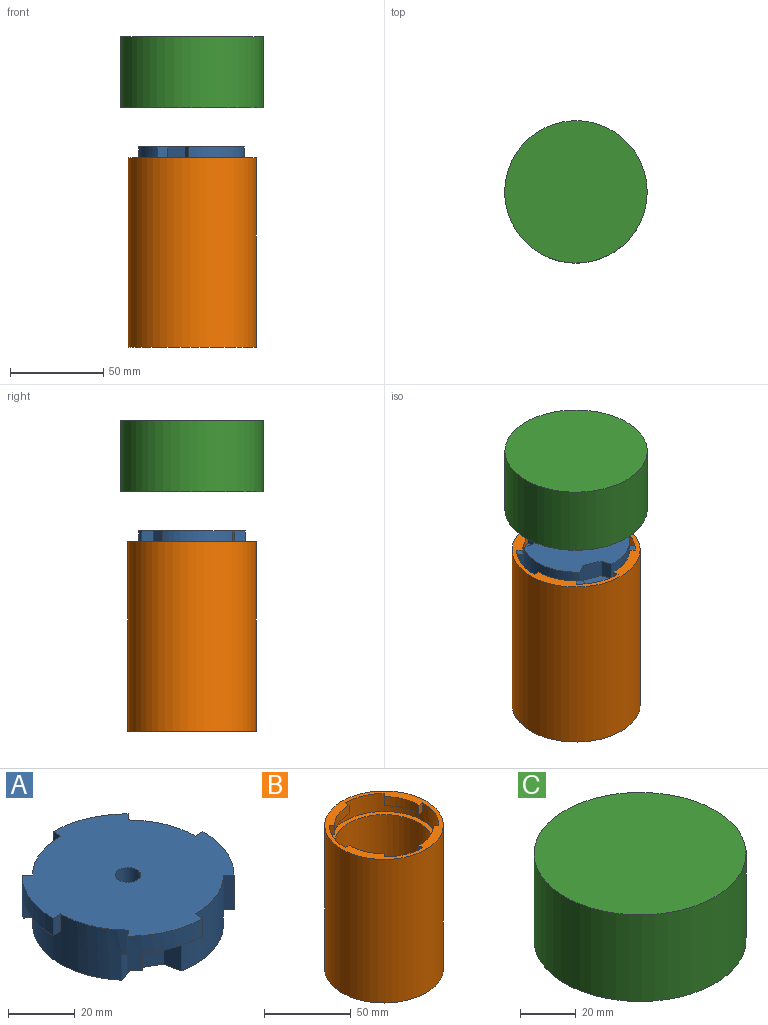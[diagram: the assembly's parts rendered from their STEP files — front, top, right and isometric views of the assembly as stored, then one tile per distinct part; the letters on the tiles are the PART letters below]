
ASSEMBLY  parts=3 mates=2
PART A: 43 faces, bbox 63.5x63.5x18.4 mm
  f0: cylinder r=28.57mm len=57.15mm, axis (0,0,-1), area 1491.7mm2, adj f2,f3,f8,f9,f11,f12,f18,f19
  f1: cylinder r=28.57mm len=39.03mm, axis (0,0,-1), area 629.9mm2, adj f4,f14,f15,f18,f20,f21,f27,f28
  f2: plane 19.11x8.93mm, normal (0,0,-1), area 61.8mm2, adj f0,f24,f32,f35
  f3: plane 19.11x8.93mm, normal (0,0,-1), area 61.8mm2, adj f0,f7,f30,f41
  f4: plane 19.11x8.93mm, normal (0,0,-1), area 61.8mm2, adj f1,f5,f28,f37
  f5: cylinder r=31.75mm len=22.45mm, axis (0,0,-1), area 186.5mm2, adj f4,f21,f28,f31,f37,f39
  f6: cylinder r=31.75mm len=22.45mm, axis (0,0,-1), area 186.5mm2, adj f21,f23,f26,f29,f33,f34
  f7: cylinder r=31.75mm len=22.45mm, axis (0,0,-1), area 186.5mm2, adj f3,f21,f27,f30,f41,f42
  f8: plane 9.53x6.24mm, normal (-0.98,-0.18,0), area 60.5mm2, adj f0,f17,f18,f20
  f9: plane 9.53x4.83mm, normal (0.65,0.76,0), area 60.5mm2, adj f0,f10,f18,f19
  f10: plane 10.16x9.53mm, normal (1,0,0), area 96.8mm2, adj f9,f11,f18,f19
  f11: plane 9.53x4.83mm, normal (0.65,-0.76,0), area 60.5mm2, adj f0,f10,f18,f19
  f12: plane 9.53x6.24mm, normal (-0.98,0.18,0), area 60.5mm2, adj f0,f13,f18,f22
  f13: plane 9.53x8.8mm, normal (-0.5,0.87,0), area 96.8mm2, adj f12,f14,f18,f22
  f14: plane 9.53x5.99mm, normal (0.33,0.94,0), area 60.5mm2, adj f1,f13,f18,f22,f38
  f15: plane 9.53x5.99mm, normal (0.33,-0.94,0), area 60.5mm2, adj f1,f17,f18,f20
  f16: cylinder r=3.81mm len=18.42mm, axis (0,0,-1), area 440.8mm2, adj f18,f21
  f17: plane 9.53x8.8mm, normal (-0.5,-0.87,0), area 96.8mm2, adj f8,f15,f18,f20
  f18: plane 57.15x55.63mm, normal (0,0,-1), area 2256.3mm2, adj f0,f1,f8,f9,f10,f11,f12,f13
  f19: plane 18.41x6.35mm, normal (0,0,-1), area 87.8mm2, adj f0,f9,f10,f11
  f20: plane 15.95x11.32mm, normal (0,0,-1), area 87.8mm2, adj f0,f1,f8,f15,f17,f40
  f21: plane 63.5x63.5mm, normal (0,0,1), area 2820.5mm2, adj f0,f1,f5,f6,f7,f16,f24,f25
  f22: plane 15.95x11.32mm, normal (0,0,-1), area 87.8mm2, adj f0,f12,f13,f14,f38
  f23: plane 19.11x8.93mm, normal (0,0,-1), area 61.8mm2, adj f0,f6,f26,f33
  f24: cylinder r=31.75mm len=22.45mm, axis (0,0,-1), area 186.5mm2, adj f2,f21,f25,f32,f35,f36
  f25: plane 12.7x2.25mm, normal (0.71,-0.71,0), area 40.3mm2, adj f0,f21,f24,f36
  f26: plane 6.35x3.18mm, normal (0,1,0), area 20.2mm2, adj f0,f6,f21,f23
  f27: plane 12.7x2.25mm, normal (-0.71,0.71,0), area 40.3mm2, adj f1,f7,f21,f40,f42
  f28: plane 6.35x3.18mm, normal (0,-1,0), area 20.2mm2, adj f1,f4,f5,f21
  f29: plane 12.7x2.25mm, normal (-0.71,-0.71,0), area 40.3mm2, adj f0,f6,f21,f34
  f30: plane 6.35x3.18mm, normal (1,0,0), area 20.2mm2, adj f0,f3,f7,f21
  f31: plane 12.7x2.25mm, normal (0.71,0.71,0), area 40.3mm2, adj f0,f5,f21,f38,f39
  f32: plane 6.35x3.18mm, normal (-1,0,0), area 20.2mm2, adj f0,f2,f21,f24
  f33: plane 6.35x2.54mm, normal (0.6,0.8,0), area 20.2mm2, adj f0,f6,f23,f34
  f34: plane 5.25x5.15mm, normal (0,0,-1), area 13.4mm2, adj f0,f6,f29,f33
  f35: plane 6.35x2.54mm, normal (-0.8,0.6,0), area 20.2mm2, adj f0,f2,f24,f36
  f36: plane 5.25x5.15mm, normal (0,0,-1), area 13.4mm2, adj f0,f24,f25,f35
  f37: plane 6.35x2.54mm, normal (-0.6,-0.8,0), area 20.2mm2, adj f1,f4,f5,f39
  f38: cylinder r=28.57mm len=3.81mm, axis (0,0,1), area 7.2mm2, adj f14,f22,f31,f39
  f39: plane 5.25x5.15mm, normal (0,0,-1), area 13.4mm2, adj f1,f5,f31,f37,f38
  f40: cylinder r=28.57mm len=3.81mm, axis (0,0,1), area 15.2mm2, adj f20,f27,f41,f42
  f41: plane 6.35x2.54mm, normal (0.8,-0.6,0), area 20.2mm2, adj f0,f3,f7,f40,f42
  f42: plane 5.25x5.15mm, normal (0,0,-1), area 13.4mm2, adj f7,f27,f40,f41
PART B: 23 faces, bbox 68.6x68.6x101.6 mm
  f0: cylinder r=28.57mm len=85.73mm, axis (0,0,1), area 15391.2mm2, adj f13,f22
  f1: cylinder r=28.57mm len=20.21mm, axis (0,0,1), area 142.5mm2, adj f4,f10,f19,f20
  f2: cylinder r=28.57mm len=20.21mm, axis (0,0,1), area 142.5mm2, adj f5,f10,f17,f18
  f3: cylinder r=28.57mm len=20.21mm, axis (0,0,1), area 142.5mm2, adj f6,f10,f15,f16
  f4: plane 22.45x11.54mm, normal (0,0,-1), area 75.2mm2, adj f1,f12,f19,f20
  f5: plane 22.45x11.54mm, normal (0,0,-1), area 75.2mm2, adj f2,f12,f17,f18
  f6: plane 22.45x11.54mm, normal (0,0,-1), area 75.2mm2, adj f3,f12,f15,f16
  f7: cylinder r=28.57mm len=20.21mm, axis (0,0,1), area 142.5mm2, adj f10,f11,f14,f21
  f8: cylinder r=34.29mm len=101.6mm, axis (0,0,1), area 21889.8mm2, adj f9,f10
  f9: plane 68.58x68.58mm, normal (0,0,-1), area 3693.9mm2, adj f8
  f10: plane 68.58x68.58mm, normal (0,0,1), area 827.8mm2, adj f1,f2,f3,f7,f8,f12,f14,f15
  f11: plane 22.45x11.54mm, normal (0,0,-1), area 75.2mm2, adj f7,f12,f14,f21
  f12: cylinder r=31.75mm len=63.5mm, axis (0,0,-1), area 1900.2mm2, adj f4,f5,f6,f10,f11,f13,f14,f15
  f13: plane 63.5x63.5mm, normal (0,0,1), area 601.7mm2, adj f0,f12
  f14: plane 6.35x2.25mm, normal (-0.71,0.71,0), area 20.2mm2, adj f7,f10,f11,f12
  f15: plane 6.35x3.18mm, normal (1,0,0), area 20.2mm2, adj f3,f6,f10,f12
  f16: plane 6.35x2.25mm, normal (-0.71,-0.71,0), area 20.2mm2, adj f3,f6,f10,f12
  f17: plane 6.35x3.18mm, normal (0,1,0), area 20.2mm2, adj f2,f5,f10,f12
  f18: plane 6.35x2.25mm, normal (0.71,-0.71,0), area 20.2mm2, adj f2,f5,f10,f12
  f19: plane 6.35x3.18mm, normal (-1,0,0), area 20.2mm2, adj f1,f4,f10,f12
  f20: plane 6.35x2.25mm, normal (0.71,0.71,0), area 20.2mm2, adj f1,f4,f10,f12
  f21: plane 6.35x3.18mm, normal (0,-1,0), area 20.2mm2, adj f7,f10,f11,f12
  f22: plane 57.15x57.15mm, normal (0,0,1), area 2565.2mm2, adj f0
PART C: 19 faces, bbox 76.2x76.2x38.1 mm
  f0: cylinder r=28.57mm len=57.15mm, axis (0,0,1), area 3063.1mm2, adj f4,f5,f7,f9,f10,f12,f13,f14
  f1: plane 76.2x76.2mm, normal (0,0,1), area 4560.4mm2, adj f6
  f2: plane 7.62x7.62mm, normal (0,0,-1), area 45.6mm2, adj f3
  f3: cylinder r=3.81mm len=19.05mm, axis (0,0,1), area 456mm2, adj f2,f4
  f4: plane 57.15x55.63mm, normal (0,0,-1), area 2256.3mm2, adj f0,f3,f7,f8,f9,f11,f12,f13
  f5: plane 76.2x76.2mm, normal (0,0,-1), area 1995.2mm2, adj f0,f6
  f6: cylinder r=38.1mm len=76.2mm, axis (0,0,1), area 9120.7mm2, adj f1,f5
  f7: plane 6.35x4.83mm, normal (-0.65,-0.76,0), area 40.3mm2, adj f0,f4,f8,f10
  f8: plane 10.16x6.35mm, normal (-1,0,0), area 64.5mm2, adj f4,f7,f9,f10
  f9: plane 6.35x4.83mm, normal (-0.65,0.76,0), area 40.3mm2, adj f0,f4,f8,f10
  f10: plane 18.41x6.35mm, normal (0,0,-1), area 87.8mm2, adj f0,f7,f8,f9
  f11: plane 8.8x6.35mm, normal (0.5,-0.87,0), area 64.5mm2, adj f4,f12,f13,f14
  f12: plane 6.35x5.99mm, normal (-0.33,-0.94,0), area 40.3mm2, adj f0,f4,f11,f14
  f13: plane 6.35x6.24mm, normal (0.98,-0.18,0), area 40.3mm2, adj f0,f4,f11,f14
  f14: plane 15.95x11.32mm, normal (0,0,-1), area 87.8mm2, adj f0,f11,f12,f13
  f15: plane 8.8x6.35mm, normal (0.5,0.87,0), area 64.5mm2, adj f4,f16,f17,f18
  f16: plane 6.35x6.24mm, normal (0.98,0.18,0), area 40.3mm2, adj f0,f4,f15,f18
  f17: plane 6.35x5.99mm, normal (-0.33,0.94,0), area 40.3mm2, adj f0,f4,f15,f18
  f18: plane 15.95x11.32mm, normal (0,0,-1), area 87.8mm2, adj f0,f15,f16,f17
PLACE A rot(axis=(1,0.07,0),180deg) t=(28.8,-65.16,17.31)mm
PLACE B t=(28.8,-65.16,11.59)mm
PLACE C rot(axis=(0,0,1),8deg) t=(28.8,-65.16,57.38)mm
MATE cylindrical A.f0 <-> B.f0  axis (0,0,1) through (28.8,-65.16,17.31)mm
MATE cylindrical C.f0 <-> A.f0  axis (0,0,-1) through (28.8,-65.16,38.33)mm
